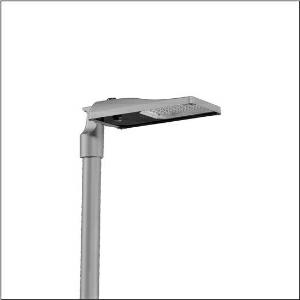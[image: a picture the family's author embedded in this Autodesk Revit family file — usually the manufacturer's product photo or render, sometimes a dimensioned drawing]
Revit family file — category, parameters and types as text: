
# Revit family: streetlight_sl_31_mini___pl52_5xh6h31t08ha_406f
name_source: partatom
category: Lighting Fixtures
units: mm (PartAtom-declared; Revit-internal decimal feet)

## family parameters
Cut with Voids When Loaded = No
Host = Face
Light Source = No
Part Type = Normal
Room Calculation Point = No
Round Connector Dimension = Use Diameter
Shared = No

## types (1)
- --- (1 x LED, 9070 lm, 68.3 W, 3000K)
    Apparent Load = 68 VA
    CIE Flux Codes = 27 59 98 100 100
    Color Rendering = 70
    Color Temperature = 3000K
    Default Elevation = 1800 mm
    Description = Streetlight SL 31 mini D4i, Desk-Remote mast luminaire for post-top, side-entry; light control with lens of PMMA; light distribution: PL52, direct asymmetric distribution, for standard-compliant lighting for roads and squares; LED: luminous flux: 9.070lm, light colour: 730, colour temperature: 3000K; luminous efficacy: 132,8lm/W; control: pre-setting: logarithmic dimming characteristic, flexible luminous flux parameterisation, time-dependent luminous flux control, constant luminous flux control, power reduction, intelligent temperature release in ECG and LED module, overheat protection; luminaire housing, of diecast aluminium, Siteco® metallic grey (DB 702S), corrosivity category C5 high according to DIN EN ISO 12944; cover of toughened safety glass, transparent, opened without tools; mast flange of diecast aluminium, Siteco® metallic grey (DB 702S), spigot size: 76/60mm, mast flange included unmounted; with cable H07RN-F 2x 1.5mm², cable length: 8,5m, connection cable pre-assembled; mains connection: 220..240V, AC, 50/60Hz; power consumption (at start of service life): 68,3W / (at end of service life): 74,5W / (with reduced operation 50%): 29,5W; protection rating (complete): IP66; insulation class (complete): insulation class II (safety insulation); impact resistance: IK09; certification: CE, ENEC, ENEC+, VDE, UKCA, ZD4i; permissible operating ambient temperature for outdoor applications: -40..+50°C; packaging unit: 1 piece

Light Distribution: PL52
    Height = 76 mm
    Lamp = 1 x LED
    Lamp Light Flux = 9070 lm
    Lamp Power = 68.3 W
    Lamp count = 1
    Length = 547 mm
    Luminous efficacy = 133 lm/W
    Manufacturer = Siteco
    ModVariant = No
    Model = 5XH6H31T08HA
    Number of Poles = 1
    OnlyDefault = Yes
    Power Factor = 1
    Product Name = Streetlight SL 31 mini | PL52
    Product group = mast luminaire | pylon top
    ProductGroupID = 6100
    Protection Class = Protection class II
    Protection Degree = IP 66
    RLX_Detail_Level = 1
    RLX_Emergency_Light_Flux = 0 lm
    RLX_Emergency_Type = 0
    RLX_Emergency_Type_DB = No
    RlxData = <blob elided: 33861 chars, md5=71a67ad6>
    Socket = socket
    Standby Power = 0 W
    System Light Flux = 9070 lm
    System Power = 68 W
    Type Comments = factory setting: luminous flux: 100 % | dim-lin: 254 | 692 mA
    Type Image = l_1300332.jpg
    URL = http://relux.com
    VarID = @adj_002439
    Voltage = 0 V
    Weight = 0.00 kg
    Width = 265 mm

## geometry (parser evidence)
native form markers: Blend x4, Sweep x11
no freeform markers — native parametric forms only
